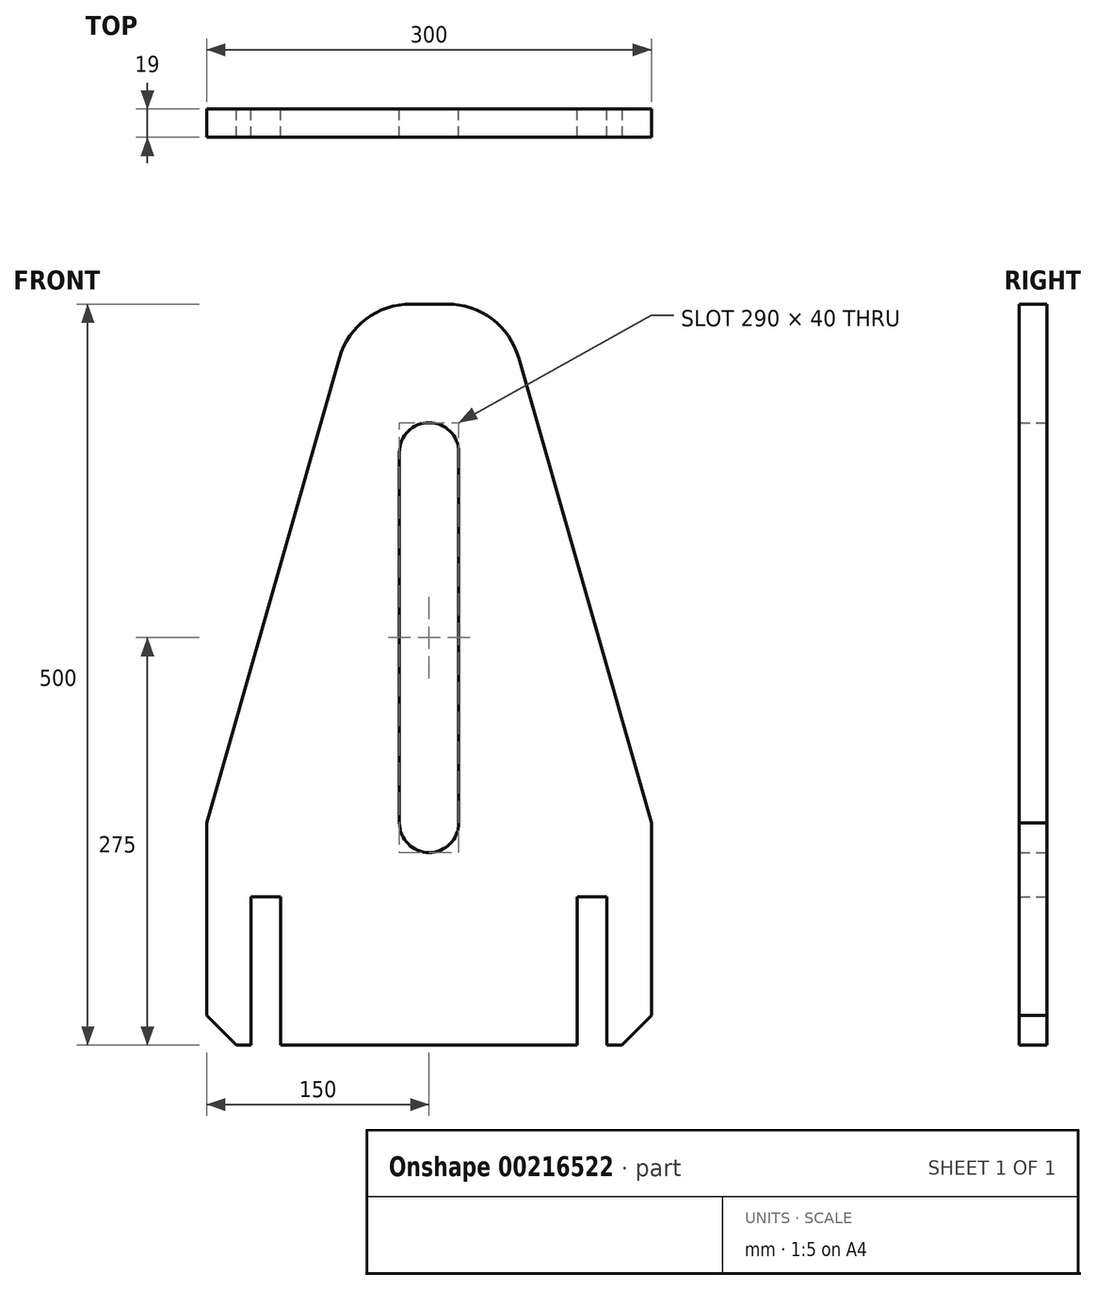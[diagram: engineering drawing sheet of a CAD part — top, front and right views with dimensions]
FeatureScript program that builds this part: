
annotation { "Feature Type Name" : "Feature", "Feature Type Description" : "" }
export const myFeature = defineFeature(function(context is Context, id is Id, definition is map)
    precondition{}
    {
        {
            var Q0;
            Q0=qCreatedBy(makeId("Front.planeOp"),FACE);
            var sketch = newSketch(context, id + "F0", { "sketchPlane" : qUnion([Q0])});
            skLineSegment(sketch, "E0.bottom", {"start": v(-150, 250) * mm, "end": v(150, 250) * mm, "construction": true});
            skLineSegment(sketch, "E0.left", {"start": v(-150, 250) * mm, "end": v(-150, -250) * mm});
            skLineSegment(sketch, "E0.right", {"start": v(150, 250) * mm, "end": v(150, -250) * mm});
            skLineSegment(sketch, "E1.top", {"start": v(-120, -150) * mm, "end": v(-100, -150) * mm});
            skLineSegment(sketch, "E1.left", {"start": v(-120, -250) * mm, "end": v(-120, -150) * mm});
            skLineSegment(sketch, "E1.right", {"start": v(-100, -250) * mm, "end": v(-100, -150) * mm});
            skLineSegment(sketch, "E2", {"start": v(0, 250) * mm, "end": v(0, -250) * mm, "construction": true});
            skLineSegment(sketch, "E3.MirrorCS", {"start": v(120, -250) * mm, "end": v(120, -150) * mm});
            skLineSegment(sketch, "E4.MirrorCS", {"start": v(120, -150) * mm, "end": v(100, -150) * mm});
            skLineSegment(sketch, "E5.MirrorCS", {"start": v(100, -250) * mm, "end": v(100, -150) * mm});
            skLineSegment(sketch, "E6.trimOffspring", {"start": v(120, -250) * mm, "end": v(150, -250) * mm});
            skLineSegment(sketch, "E7.trimOffspring", {"start": v(-100, -250) * mm, "end": v(0, -250) * mm});
            skLineSegment(sketch, "E8", {"start": v(-150, -250) * mm, "end": v(-120, -250) * mm});
            skLineSegment(sketch, "E9", {"start": v(0, -250) * mm, "end": v(100, -250) * mm});
            skLineSegment(sketch, "E10", {"start": v(-150, 250) * mm, "end": v(0, 250) * mm});
            skLineSegment(sketch, "E11.MirrorCS", {"start": v(150, 250) * mm, "end": v(0, 250) * mm});
            skArc(sketch, "E12", {"start": v(20, 150) * mm, "mid": v(0, 170) * mm, "end": v(-20, 150) * mm});
            skArc(sketch, "E13", {"start": v(-20, -100) * mm, "mid": v(0, -120) * mm, "end": v(20, -100) * mm});
            skLineSegment(sketch, "E14", {"start": v(-20, 150) * mm, "end": v(-20, -100) * mm});
            skLineSegment(sketch, "E15", {"start": v(20, 150) * mm, "end": v(20, -100) * mm});
            skSolve(sketch);
        }
        {
            var Q0;
            Q0=makeQuery(id+"F0.imprint","IMPRINT",FACE,{"disambiguationData":[TD([[makeQuery(id+"F0.imprint","IMPRINT",EDGE,{"derivedFrom":sQuery(id+"F0.wireOp",EDGE,"E0.left")}),1.0]])]});
            extrude(context, id + "F1", {"entities" : qUnion([Q0]), "depth" : 19 * mm, "symmetric" : true});
        }
        {
            var Q0;
            Q0=makeQuery(id+"F1.opExtrude","SWEPT_EDGE",EDGE,{"disambiguationData":[OSD([sQuery(id+"F0.wireOp",EDGE,"E0.right"),sQuery(id+"F0.wireOp",EDGE,"E11.MirrorCS")])]});
            var Q1;
            Q1=makeQuery(id+"F1.opExtrude","SWEPT_EDGE",EDGE,{"disambiguationData":[OSD([sQuery(id+"F0.wireOp",EDGE,"E0.left"),sQuery(id+"F0.wireOp",EDGE,"E10")])]});
            chamfer(context, id + "F2", {"entities" : qUnion([Q0, Q1]), "chamferType" : ChamferType.TWO_OFFSETS, "width1" : 100 * mm, "oppositeDirection" : false, "width2" : 350 * mm, "tangentPropagation" : true});
        }
        {
            var Q0;
            {var subQ0=sQuery(id+"F0.wireOp",EDGE,"E10");Q0=makeQuery(id+"F2.opChamfer","BLEND_EDGE",EDGE,{"blendedFrom":[makeQuery(id+"F1.opExtrude","SWEPT_EDGE",EDGE,{"disambiguationData":[OSD([sQuery(id+"F0.wireOp",EDGE,"E0.left"),subQ0])]}),makeQuery(id+"F1.opExtrude","SWEPT_FACE",FACE,{"disambiguationData":[OSD([subQ0,sQuery(id+"F0.wireOp",EDGE,"E11.MirrorCS")])]})],"blendedInto":[makeQuery(id+"F1.opExtrude","SWEPT_FACE",FACE,{"disambiguationData":[OSD([subQ0,sQuery(id+"F0.wireOp",EDGE,"E11.MirrorCS")])]})]});}
            var Q1;
            {var subQ0=sQuery(id+"F0.wireOp",EDGE,"E11.MirrorCS");Q1=makeQuery(id+"F2.opChamfer","BLEND_EDGE",EDGE,{"blendedFrom":[makeQuery(id+"F1.opExtrude","SWEPT_EDGE",EDGE,{"disambiguationData":[OSD([sQuery(id+"F0.wireOp",EDGE,"E0.right"),subQ0])]}),makeQuery(id+"F1.opExtrude","SWEPT_FACE",FACE,{"disambiguationData":[OSD([sQuery(id+"F0.wireOp",EDGE,"E10"),subQ0])]})],"blendedInto":[makeQuery(id+"F1.opExtrude","SWEPT_FACE",FACE,{"disambiguationData":[OSD([sQuery(id+"F0.wireOp",EDGE,"E10"),subQ0])]})]});}
            fillet(context, id + "F3", {"entities" : qUnion([Q0, Q1]), "radius" : 50 * mm, "tangentPropagation" : true, "allowEdgeOverflow" : false});
        }
        {
            var Q0;
            Q0=makeQuery(id+"F1.opExtrude","SWEPT_EDGE",EDGE,{"disambiguationData":[OSD([sQuery(id+"F0.wireOp",EDGE,"E0.left"),sQuery(id+"F0.wireOp",EDGE,"E8")])]});
            var Q1;
            Q1=makeQuery(id+"F1.opExtrude","SWEPT_EDGE",EDGE,{"disambiguationData":[OSD([sQuery(id+"F0.wireOp",EDGE,"E0.right"),sQuery(id+"F0.wireOp",EDGE,"E6.trimOffspring")])]});
            chamfer(context, id + "F4", {"entities" : qUnion([Q0, Q1]), "width" : 20 * mm, "tangentPropagation" : true});
        }
    });
